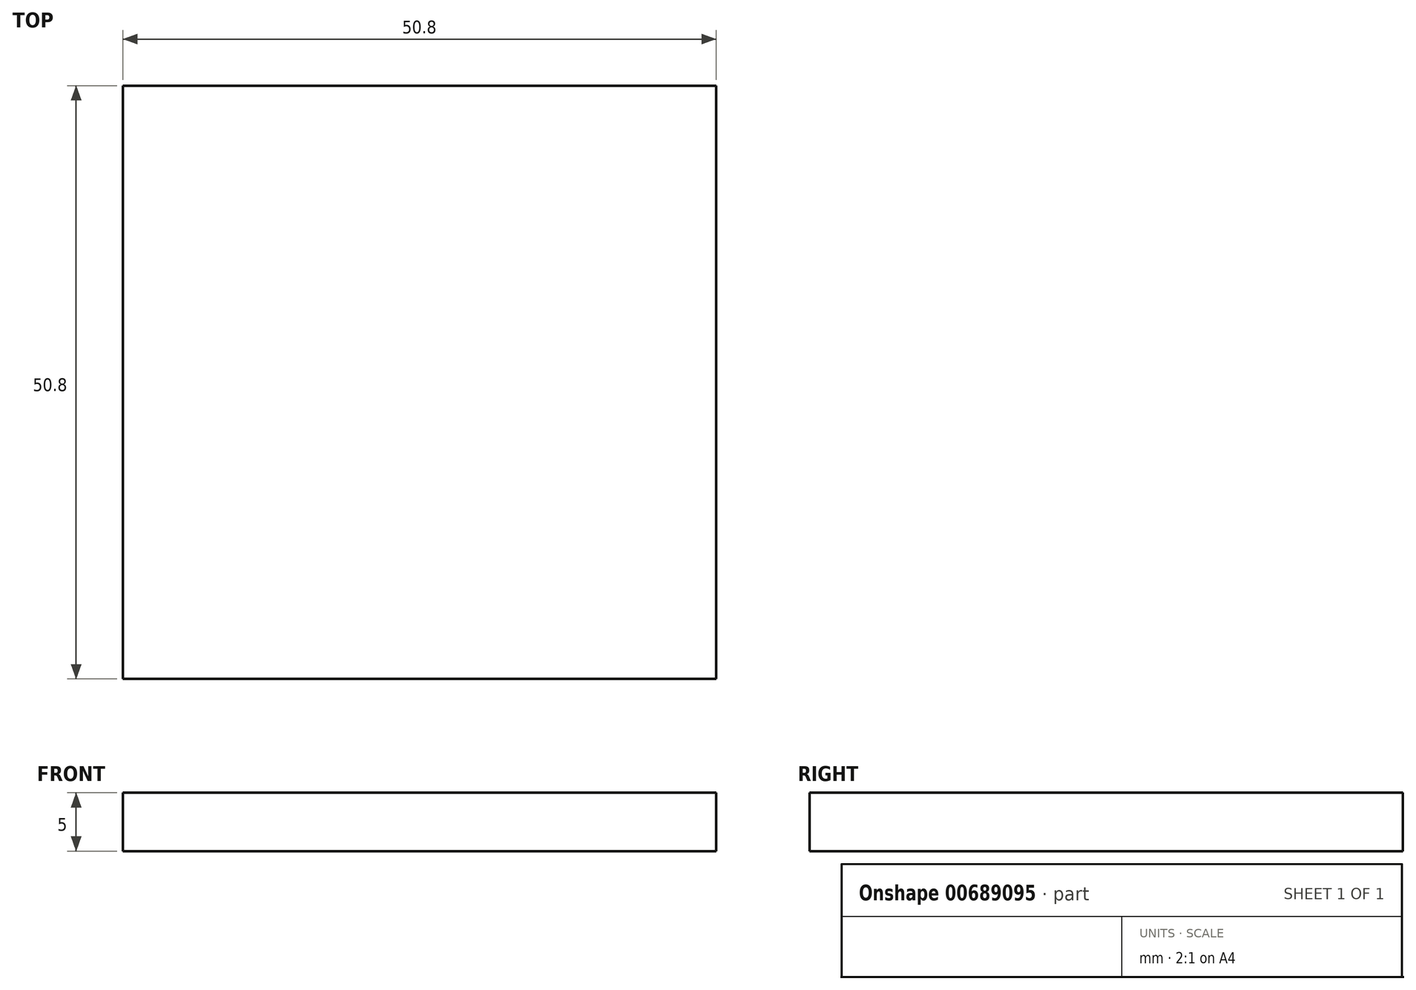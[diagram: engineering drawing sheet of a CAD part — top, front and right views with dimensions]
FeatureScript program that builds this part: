
annotation { "Feature Type Name" : "Feature", "Feature Type Description" : "" }
export const myFeature = defineFeature(function(context is Context, id is Id, definition is map)
    precondition{}
    {
        {
            var Q0;
            Q0=qCreatedBy(makeId("Top.planeOp"),FACE);
            var sketch = newSketch(context, id + "F0", { "sketchPlane" : qUnion([Q0])});
            skLineSegment(sketch, "E0.bottom", {"start": v(-25.4, -25.4) * mm, "end": v(25.4, -25.4) * mm});
            skLineSegment(sketch, "E0.top", {"start": v(-25.4, 25.4) * mm, "end": v(25.4, 25.4) * mm});
            skLineSegment(sketch, "E0.left", {"start": v(-25.4, -25.4) * mm, "end": v(-25.4, 25.4) * mm});
            skLineSegment(sketch, "E0.right", {"start": v(25.4, -25.4) * mm, "end": v(25.4, 25.4) * mm});
            skSolve(sketch);
        }
        {
            var Q0;
            Q0 = qSketchRegion(id + "F0", true);
            extrude(context, id + "F1", {"entities" : qUnion([Q0]), "depth" : 5 * mm, "offsetDistance" : 25.4 * mm});
        }
    });
